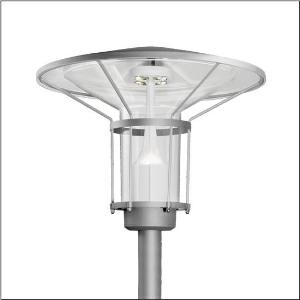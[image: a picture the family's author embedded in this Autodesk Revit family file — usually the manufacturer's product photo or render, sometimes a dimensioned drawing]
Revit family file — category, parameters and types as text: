
# Revit family: laterne_classic_iq___p1_0a_5xa5245lf14hp_1a7c
name_source: partatom
category: Lighting Fixtures
units: mm (PartAtom-declared; Revit-internal decimal feet)

## family parameters
Cut with Voids When Loaded = No
Host = Face
Light Source = No
Part Type = Normal
Room Calculation Point = No
Round Connector Dimension = Use Diameter
Shared = No

## types (1)
- --- (1 x LED, 4400 lm, 33.6 W, 4000K)
    Apparent Load = 34 VA
    CIE Flux Codes = 31 61 91 96 100
    Color Rendering = 70
    Color Temperature = 4000K
    Default Elevation = 1800 mm
    Description = Lantern Classic iQ, mast luminaire, Module 540 iQ-SR, primary light control with 3 zone facetted reflector, of plastic, silver coated, highly specular, structured, primary optical cover: cover, of PMMA, transparent, light distribution: P1.0a, light emission: direct distribution, primary light characteristic: strongly asymmetric, installation type: post-top, LED, High Power LED, rated luminous flux: 4.400lm, luminous efficacy: 131lm/W, light colour: 740, colour temperature: 4000K, control gear: ECG iQ, control: presetting dimming logarithmic, Street-Remote, Auto-Match, Temp-Guard, Lumen-Switch, Night-Set, Smart-Wire, Light-Fading, Desk-Remote (wireless, voltage-free reading and setting of iQ features in the workshop via application-optimized NFC function/RFID function), optimised constant luminous flux control (CLO 2.0), with terminal, 6-pole, max. 2.5mm², mains connection: 230..240V, AC, 50/60Hz, start of lifetime: 34W, end of service life: 36W, reduction: 15W, luminaire housing, upper part, of glass-fibre reinforced polyester, coated, Siteco® metallic grey (DB 702S), diameter: 750mm, height: 596mm, spigot size: d x l = 76 x 70mm (post-top) | with reducer (optional accessory) 60 x 70mm, post-top mast mounting element, of diecast aluminium, coated, Siteco® metallic grey (DB 702S), Module 540 iQ-SR, traffic white (RAL 9016), equipment: Power, protection rating (complete): IP65, insulation class (complete): insulation class II (safety insulation), certification: CE, ENEC, VDE, packaging unit: 1 piece

Light Distribution: P1.0a
    Height = 596 mm
    Lamp = 1 x LED
    Lamp Light Flux = 4400 lm
    Lamp Power = 33.6 W
    Lamp count = 1
    Length = 750 mm
    Luminous efficacy = 131 lm/W
    Manufacturer = Siteco
    ModVariant = No
    Model = 5XA5245LF14HP
    Number of Poles = 1
    OnlyDefault = Yes
    Power Factor = 1
    Product Name = Laterne Classic iQ | P1.0a
    Product group = mast luminaire | pylon top
    ProductGroupID = 6100
    Protection Class = Protection class II
    Protection Degree = IP 65
    RLX_Detail_Level = 1
    RLX_Emergency_Light_Flux = 0 lm
    RLX_Emergency_Type = 0
    RLX_Emergency_Type_DB = No
    RlxData = <blob elided: 65557 chars, md5=11cd0c1d>
    Socket = socket
    Standby Power = 0 W
    System Light Flux = 4400 lm
    System Power = 34 W
    Type Comments = factory setting: luminous flux: 100 % | dim-lin: 254 | 695 mA
    Type Image = l_1006052.jpg
    URL = http://relux.com
    VarID = @adj_145771
    Voltage = 0 V
    Weight = 0.00 kg
    Width = 0 mm  [stored 0 ft]

note: [stored X ft] marks values corroborated as IEEE doubles in the binary element streams (Revit-internal decimal feet)

## geometry (parser evidence)
native form markers: Blend x4, Sweep x11
no freeform markers — native parametric forms only
